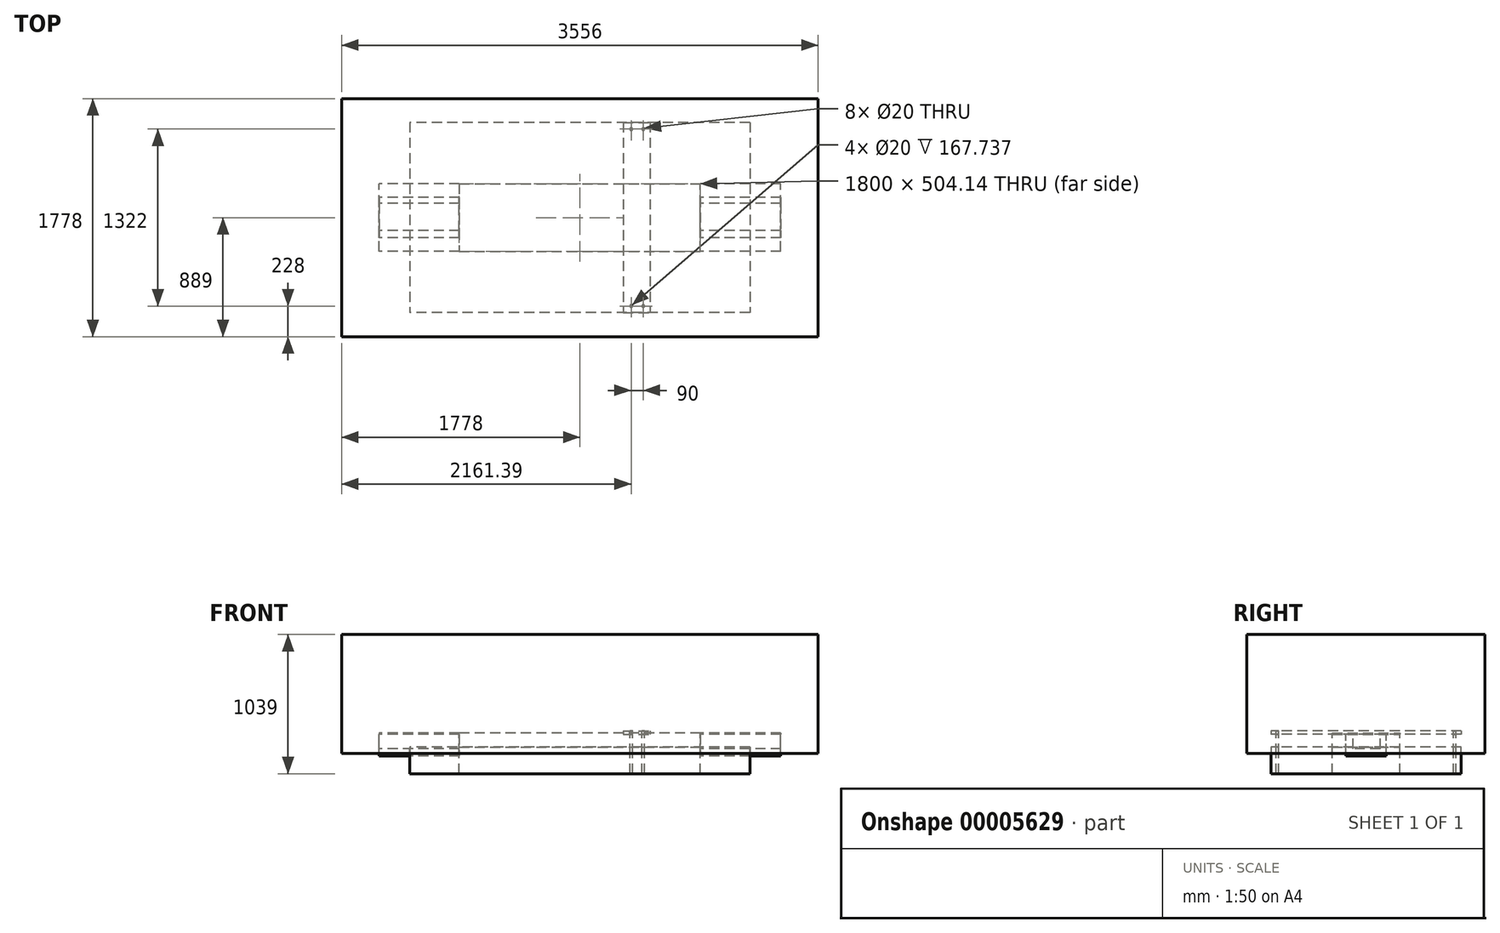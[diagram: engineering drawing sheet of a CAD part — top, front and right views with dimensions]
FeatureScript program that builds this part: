
annotation { "Feature Type Name" : "Feature", "Feature Type Description" : "" }
export const myFeature = defineFeature(function(context is Context, id is Id, definition is map)
    precondition{}
    {
        {
            var Q0;
            Q0=qCreatedBy(makeId("Top.planeOp"),FACE);
            var sketch = newSketch(context, id + "F0", { "sketchPlane" : qUnion([Q0])});
            skLineSegment(sketch, "E0.rect.bottom", {"start": v(-1778, 889) * mm, "end": v(1778, 889) * mm});
            skLineSegment(sketch, "E0.rect.top", {"start": v(-1778, -889) * mm, "end": v(1778, -889) * mm});
            skLineSegment(sketch, "E0.rect.left", {"start": v(-1778, 889) * mm, "end": v(-1778, -889) * mm});
            skLineSegment(sketch, "E0.rect.right", {"start": v(1778, 889) * mm, "end": v(1778, -889) * mm});
            skPoint(sketch, "E0.rect.middle", {"position": v(0, 0) * mm});
            skSolve(sketch);
        }
        {
            var Q0;
            Q0=makeQuery(id+"F0.imprint","IMPRINT",FACE,{"disambiguationData":[TD([[makeQuery(id+"F0.imprint","IMPRINT",EDGE,{"derivedFrom":sQuery(id+"F0.wireOp",EDGE,"E0.rect.bottom")}),-1.0]])]});
            extrude(context, id + "F1", {"entities" : qUnion([Q0]), "depth" : 889 * mm});
        }
        {
            var Q0;
            Q0=qCreatedBy(makeId("Right.planeOp"),FACE);
            var sketch = newSketch(context, id + "F2", { "sketchPlane" : qUnion([Q0])});
            skLineSegment(sketch, "E1", {"start": v(-711, 50) * mm, "end": v(-711, -150) * mm});
            skLineSegment(sketch, "E2", {"start": v(-711, -150) * mm, "end": v(711, -150) * mm});
            skLineSegment(sketch, "E3", {"start": v(711, -150) * mm, "end": v(711, 50) * mm});
            skLineSegment(sketch, "E4", {"start": v(711, 50) * mm, "end": v(-711, 50) * mm});
            skSolve(sketch);
        }
        {
            var Q0;
            Q0=makeQuery(id+"F2.imprint","IMPRINT",FACE,{"disambiguationData":[TD([[makeQuery(id+"F2.imprint","IMPRINT",EDGE,{"derivedFrom":sQuery(id+"F2.wireOp",EDGE,"E1")}),1.0]])]});
            extrude(context, id + "F3", {"entities" : qUnion([Q0]), "endBound" : BoundingType.SYMMETRIC, "depth" : 2540 * mm});
        }
        {
            var Q0;
            Q0=qCreatedBy(makeId("Right.planeOp"),FACE);
            var sketch = newSketch(context, id + "F4", { "sketchPlane" : qUnion([Q0])});
            skLineSegment(sketch, "E5.rect.top", {"start": v(-152.07, -18.82) * mm, "end": v(152.07, -18.82) * mm});
            skPoint(sketch, "E5.rect.middle", {"position": v(0, -95.87) * mm});
            skLineSegment(sketch, "E6.top", {"start": v(105.36, 35.83) * mm, "end": v(-97.74, 35.83) * mm});
            skLineSegment(sketch, "E7", {"start": v(152.07, -18.82) * mm, "end": v(152.07, 142.74) * mm});
            skLineSegment(sketch, "E8", {"start": v(152.07, 142.74) * mm, "end": v(105.36, 142.74) * mm});
            skLineSegment(sketch, "E9", {"start": v(105.36, 35.83) * mm, "end": v(105.36, 142.74) * mm});
            skLineSegment(sketch, "E10", {"start": v(-97.74, 35.83) * mm, "end": v(-97.74, 142.74) * mm});
            skLineSegment(sketch, "E11", {"start": v(-97.74, 142.74) * mm, "end": v(-152.07, 142.74) * mm});
            skLineSegment(sketch, "E12", {"start": v(-152.07, -18.82) * mm, "end": v(-152.07, 142.74) * mm});
            skSolve(sketch);
        }
        {
            var Q0;
            Q0 = qSketchRegion(id + "F4", true);
            extrude(context, id + "F5", {"entities" : qUnion([Q0]), "endBound" : BoundingType.SYMMETRIC, "depth" : 3000 * mm});
        }
        {
            var Q0;
            Q0=makeQuery(id+"F5.opExtrude","CAP_FACE",FACE,{"disambiguationData":[OSD([sQuery(id+"F4.wireOp",EDGE,"E5.rect.bottom"),sQuery(id+"F4.wireOp",EDGE,"E5.rect.top"),sQuery(id+"F4.wireOp",EDGE,"E5.rect.left"),sQuery(id+"F4.wireOp",EDGE,"E5.rect.right"),sQuery(id+"F4.wireOp",EDGE,"E6.top"),sQuery(id+"F4.wireOp",EDGE,"E6.left"),sQuery(id+"F4.wireOp",EDGE,"E6.right"),sQuery(id+"F4.wireOp",EDGE,"4a0c1dbb-f801-4d96-bdda-25b3f85c16be.trimOffspring")])],"isStart":true});
            var sketch = newSketch(context, id + "F6", { "sketchPlane" : qUnion([Q0])});
            skLineSegment(sketch, "E13.rect.bottom", {"start": v(252.07, 152.25) * mm, "end": v(-252.07, 152.25) * mm});
            skLineSegment(sketch, "E13.rect.top", {"start": v(252.07, 142.77) * mm, "end": v(-252.07, 142.77) * mm});
            skLineSegment(sketch, "E13.rect.left", {"start": v(252.07, 152.25) * mm, "end": v(252.07, 142.77) * mm});
            skLineSegment(sketch, "E13.rect.right", {"start": v(-252.07, 152.25) * mm, "end": v(-252.07, 142.77) * mm});
            skPoint(sketch, "E13.rect.middle", {"position": v(0, 147.51) * mm});
            skSolve(sketch);
        }
        {
            var Q0;
            Q0=makeQuery(id+"F6.imprint","IMPRINT",FACE,{"disambiguationData":[TD([[makeQuery(id+"F6.imprint","IMPRINT",EDGE,{"derivedFrom":sQuery(id+"F6.wireOp",EDGE,"E13.rect.bottom")}),1.0]])]});
            var Q1;
            Q1=makeQuery(id+"F5.opExtrude","CAP_FACE",FACE,{"disambiguationData":[OSD([sQuery(id+"F4.wireOp",EDGE,"E5.rect.bottom"),sQuery(id+"F4.wireOp",EDGE,"E5.rect.top"),sQuery(id+"F4.wireOp",EDGE,"E5.rect.left"),sQuery(id+"F4.wireOp",EDGE,"E5.rect.right"),sQuery(id+"F4.wireOp",EDGE,"E6.top"),sQuery(id+"F4.wireOp",EDGE,"E6.left"),sQuery(id+"F4.wireOp",EDGE,"E6.right"),sQuery(id+"F4.wireOp",EDGE,"4a0c1dbb-f801-4d96-bdda-25b3f85c16be.trimOffspring")])],"isStart":false});
            extrude(context, id + "F7", {"entities" : qUnion([Q0]), "endBound" : BoundingType.UP_TO_SURFACE, "oppositeDirection" : true, "endBoundEntityFace" : qUnion([Q1]), "depth" : 2000 * mm});
        }
        {
            var Q0;
            Q0=makeQuery(id+"F7.opExtrude","SWEPT_FACE",FACE,{"disambiguationData":[OSD([sQuery(id+"F6.wireOp",EDGE,"E13.rect.bottom")])]});
            var sketch = newSketch(context, id + "F8", { "sketchPlane" : qUnion([Q0])});
            skLineSegment(sketch, "E14.rect.bottom", {"start": v(900, -252.07) * mm, "end": v(-900, -252.07) * mm});
            skLineSegment(sketch, "E14.rect.top", {"start": v(900, 252.07) * mm, "end": v(-900, 252.07) * mm});
            skLineSegment(sketch, "E14.rect.left", {"start": v(900, 252.07) * mm, "end": v(900, -252.07) * mm});
            skLineSegment(sketch, "E14.rect.right", {"start": v(-900, 252.07) * mm, "end": v(-900, -252.07) * mm});
            skPoint(sketch, "E14.rect.middle", {"position": v(0, 0) * mm});
            skSolve(sketch);
        }
        {
            var Q0;
            Q0=makeQuery(id+"F8.imprint","IMPRINT",FACE,{"disambiguationData":[TD([[makeQuery(id+"F8.imprint","IMPRINT",EDGE,{"derivedFrom":sQuery(id+"F8.wireOp",EDGE,"E14.rect.bottom")}),-1.0]])]});
            extrude(context, id + "F9", {"entities" : qUnion([Q0]), "operationType" : NewBodyOperationType.REMOVE, "endBound" : BoundingType.THROUGH_ALL, "oppositeDirection" : true, "depth" : 25 * mm});
        }
        {
            var Q0;
            Q0=makeQuery(id+"F5.opExtrude","SWEPT_FACE",FACE,{"disambiguationData":[OSD([sQuery(id+"F4.wireOp",EDGE,"E8")])]});
            var sketch = newSketch(context, id + "F10", { "sketchPlane" : qUnion([Q0])});
            skLineSegment(sketch, "E15.bottom", {"start": v(323.4, 711) * mm, "end": v(523.4, 711) * mm});
            skLineSegment(sketch, "E15.top", {"start": v(323.4, -711) * mm, "end": v(523.4, -711) * mm});
            skLineSegment(sketch, "E15.left", {"start": v(323.4, 711) * mm, "end": v(323.4, -711) * mm});
            skLineSegment(sketch, "E15.right", {"start": v(523.4, 711) * mm, "end": v(523.4, -711) * mm});
            skSolve(sketch);
        }
        {
            var Q0;
            {var subQ5=sQuery(id+"F10.wireOp",EDGE,"f7278227-003c-457f-84dd-ba670b5042c8.bottom");Q0=makeQuery(id+"F10.imprint","IMPRINT",FACE,{"disambiguationData":[TD([[makeQuery(id+"F10.imprint","IMPRINT",EDGE,{"derivedFrom":subQ5}),-1.0]])]});}
            var Q1;
            {var subQ0=sQuery(id+"F4.wireOp",EDGE,"E8");var subQ4=sQuery(id+"F10.wireOp",EDGE,"f7278227-003c-457f-84dd-ba670b5042c8.left");var subQ6=makeQuery(id+"F5.opExtrude","SWEPT_EDGE",EDGE,{"disambiguationData":[OSD([sQuery(id+"F4.wireOp",EDGE,"E7"),subQ0])]});var subQ8=makeQuery(id+"F10.imprint","INTERSECT",VERTEX,{"derivedFrom":[subQ6,subQ4]});Q1=makeQuery(id+"F10.imprint","IMPRINT",FACE,{"disambiguationData":[TD([[makeQuery(id+"F10.imprint","IMPRINT",EDGE,{"disambiguationData":[TD([[subQ8,-1.0]])],"derivedFrom":subQ4}),1.0]])]});}
            var Q2;
            {var subQ5=sQuery(id+"F10.wireOp",EDGE,"f7278227-003c-457f-84dd-ba670b5042c8.top");Q2=makeQuery(id+"F10.imprint","IMPRINT",FACE,{"disambiguationData":[TD([[makeQuery(id+"F10.imprint","IMPRINT",EDGE,{"derivedFrom":subQ5}),1.0]])]});}
            var Q3;
            {var subQ5=sQuery(id+"F10.wireOp",EDGE,"E15.bottom");Q3=makeQuery(id+"F10.imprint","IMPRINT",FACE,{"disambiguationData":[TD([[makeQuery(id+"F10.imprint","IMPRINT",EDGE,{"derivedFrom":subQ5}),-1.0]])]});}
            var Q4;
            {var subQ0=sQuery(id+"F4.wireOp",EDGE,"E8");var subQ4=sQuery(id+"F10.wireOp",EDGE,"E15.left");var subQ6=makeQuery(id+"F5.opExtrude","SWEPT_EDGE",EDGE,{"disambiguationData":[OSD([sQuery(id+"F4.wireOp",EDGE,"E7"),subQ0])]});var subQ8=makeQuery(id+"F10.imprint","INTERSECT",VERTEX,{"derivedFrom":[subQ6,subQ4]});Q4=makeQuery(id+"F10.imprint","IMPRINT",FACE,{"disambiguationData":[TD([[makeQuery(id+"F10.imprint","IMPRINT",EDGE,{"disambiguationData":[TD([[subQ8,-1.0]])],"derivedFrom":subQ4}),1.0]])]});}
            var Q5;
            {var subQ5=sQuery(id+"F10.wireOp",EDGE,"E15.top");Q5=makeQuery(id+"F10.imprint","IMPRINT",FACE,{"disambiguationData":[TD([[makeQuery(id+"F10.imprint","IMPRINT",EDGE,{"derivedFrom":subQ5}),1.0]])]});}
            extrude(context, id + "F11", {"entities" : qUnion([Q0, Q1, Q2, Q3, Q4, Q5]), "depth" : 25 * mm});
        }
        {
            var Q0;
            Q0=makeQuery(id+"F11.opExtrude","CAP_FACE",FACE,{"disambiguationData":[OSD([sQuery(id+"F10.wireOp",EDGE,"E15.bottom"),sQuery(id+"F10.wireOp",EDGE,"E15.top"),sQuery(id+"F10.wireOp",EDGE,"E15.left"),sQuery(id+"F10.wireOp",EDGE,"E15.right")])],"isStart":false});
            var sketch = newSketch(context, id + "F12", { "sketchPlane" : qUnion([Q0])});
            skCircle(sketch, "E16", {"center": v(473.4, 661) * mm, "radius": 10 * mm});
            skCircle(sketch, "E17", {"center": v(383.4, 661) * mm, "radius": 10 * mm});
            skCircle(sketch, "E18", {"center": v(473.4, -661) * mm, "radius": 10 * mm});
            skCircle(sketch, "E19", {"center": v(383.4, -661) * mm, "radius": 10 * mm});
            skSolve(sketch);
        }
        {
            var Q0;
            Q0 = qSketchRegion(id + "F12", true);
            extrude(context, id + "F13", {"entities" : qUnion([Q0]), "operationType" : NewBodyOperationType.REMOVE, "endBound" : BoundingType.THROUGH_ALL, "oppositeDirection" : true, "depth" : 25 * mm});
        }
    });
